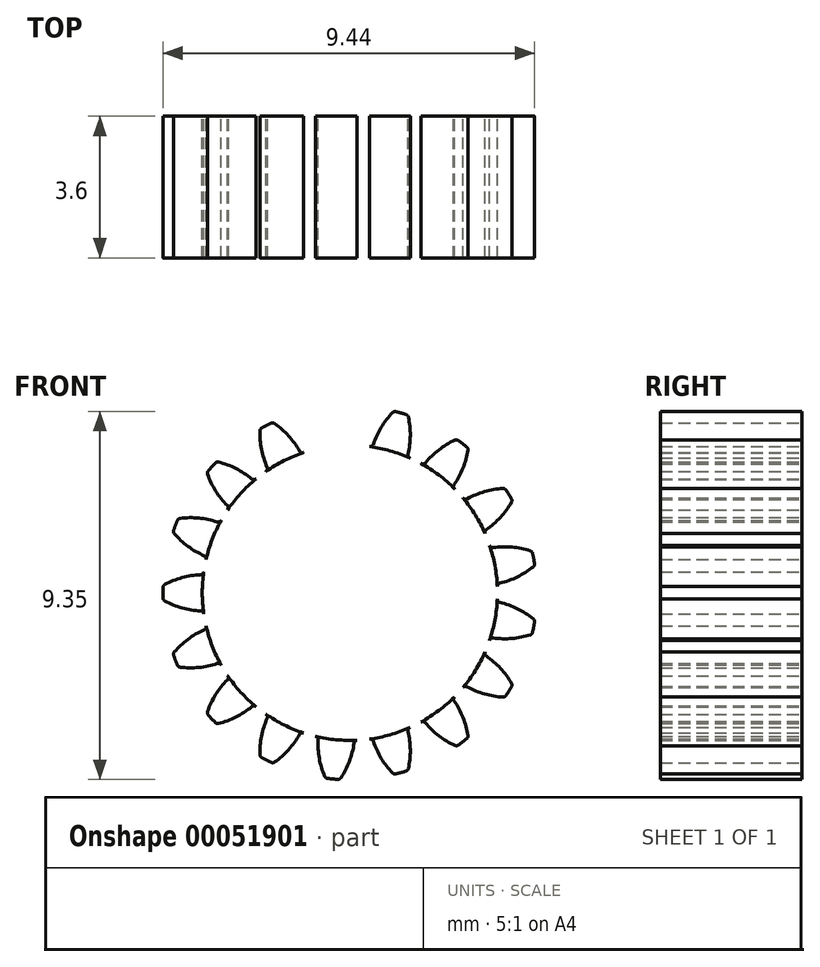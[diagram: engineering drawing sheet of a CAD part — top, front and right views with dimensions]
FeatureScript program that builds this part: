
annotation { "Feature Type Name" : "Feature", "Feature Type Description" : "" }
export const myFeature = defineFeature(function(context is Context, id is Id, definition is map)
    precondition{}
    {
        {
            var Q0;
            Q0=qCreatedBy(makeId("Front.planeOp"),FACE);
            var sketch = newSketch(context, id + "F0", { "sketchPlane" : qUnion([Q0])});
            skCircle(sketch, "E0", {"center": v(0, 0) * mm, "radius": 3.75 * mm, "construction": true});
            skCircle(sketch, "E1", {"center": v(0, 0) * mm, "radius": 4.25 * mm, "construction": true});
            skCircle(sketch, "E2", {"center": v(0, 0) * mm, "radius": 4.75 * mm, "construction": true});
            skLineSegment(sketch, "E3", {"start": v(0, 0) * mm, "end": v(0, 10.28) * mm, "construction": true});
            skLineSegment(sketch, "E4", {"start": v(0, 0) * mm, "end": v(-1.03, 11.12) * mm, "construction": true});
            skLineSegment(sketch, "E5", {"start": v(0, 4.25) * mm, "end": v(-15.76, 4.25) * mm, "construction": true});
            skLineSegment(sketch, "E6", {"start": v(0, 4.25) * mm, "end": v(-14.39, -0.99) * mm, "construction": true});
            skCircle(sketch, "E7", {"center": v(0, 4.25) * mm, "radius": 2.12 * mm, "construction": true});
            skCircle(sketch, "E8", {"center": v(-2, 3.52) * mm, "radius": 2.12 * mm, "construction": true});
            skArc(sketch, "E9", {"start": v(-0.23, 4.7) * mm, "mid": v(-0.01, 4.28) * mm, "end": v(0.1, 3.82) * mm});
            skArc(sketch, "E10.MirrorCS", {"start": v(-0.64, 4.66) * mm, "mid": v(-0.78, 4.2) * mm, "end": v(-0.8, 3.73) * mm});
            skArc(sketch, "E11", {"start": v(-0.57, 4.72) * mm, "mid": v(-0.44, 4.73) * mm, "end": v(-0.3, 4.74) * mm});
            skArc(sketch, "E12", {"start": v(-0.87, 3.65) * mm, "mid": v(0.35, -3.73) * mm, "end": v(0.19, 3.75) * mm});
            skPoint(sketch, "E13.visualSharp", {"position": v(-0.8, 3.66) * mm});
            skArc(sketch, "E13.filletArc", {"start": v(-0.87, 3.65) * mm, "mid": v(-0.82, 3.68) * mm, "end": v(-0.8, 3.73) * mm});
            skPoint(sketch, "E14.visualSharp", {"position": v(-0.62, 4.7) * mm});
            skArc(sketch, "E14.filletArc", {"start": v(-0.57, 4.72) * mm, "mid": v(-0.61, 4.7) * mm, "end": v(-0.64, 4.66) * mm});
            skPoint(sketch, "E15.visualSharp", {"position": v(-0.26, 4.74) * mm});
            skArc(sketch, "E15.filletArc", {"start": v(-0.23, 4.7) * mm, "mid": v(-0.26, 4.73) * mm, "end": v(-0.3, 4.74) * mm});
            skPoint(sketch, "E16.visualSharp", {"position": v(0.12, 3.75) * mm});
            skArc(sketch, "E16.filletArc", {"start": v(0.1, 3.82) * mm, "mid": v(0.13, 3.77) * mm, "end": v(0.19, 3.75) * mm});
            skArc(sketch, "E17.1.0", {"start": v(-2.13, 3.09) * mm, "mid": v(-2.1, 3.13) * mm, "end": v(-2.1, 3.19) * mm});
            skArc(sketch, "E17.1.1", {"start": v(-2.28, 4.12) * mm, "mid": v(-2.24, 3.64) * mm, "end": v(-2.1, 3.19) * mm});
            skArc(sketch, "E17.1.2", {"start": v(-2.24, 4.2) * mm, "mid": v(-2.27, 4.16) * mm, "end": v(-2.28, 4.12) * mm});
            skArc(sketch, "E17.1.3", {"start": v(-2.24, 4.2) * mm, "mid": v(-2.12, 4.25) * mm, "end": v(-2, 4.3) * mm});
            skArc(sketch, "E17.1.4", {"start": v(-1.91, 4.3) * mm, "mid": v(-1.95, 4.32) * mm, "end": v(-2, 4.3) * mm});
            skArc(sketch, "E17.1.5", {"start": v(-1.91, 4.3) * mm, "mid": v(-1.56, 3.99) * mm, "end": v(-1.28, 3.6) * mm});
            skArc(sketch, "E17.1.6", {"start": v(-1.28, 3.6) * mm, "mid": v(-1.24, 3.56) * mm, "end": v(-1.18, 3.56) * mm});
            skArc(sketch, "E17.2.0", {"start": v(-3.1, 2.1) * mm, "mid": v(-3.09, 2.16) * mm, "end": v(-3.11, 2.22) * mm});
            skArc(sketch, "E17.2.1", {"start": v(-3.61, 3.02) * mm, "mid": v(-3.4, 2.59) * mm, "end": v(-3.11, 2.22) * mm});
            skArc(sketch, "E17.2.2", {"start": v(-3.6, 3.1) * mm, "mid": v(-3.62, 3.06) * mm, "end": v(-3.61, 3.02) * mm});
            skArc(sketch, "E17.2.3", {"start": v(-3.6, 3.1) * mm, "mid": v(-3.51, 3.2) * mm, "end": v(-3.42, 3.3) * mm});
            skArc(sketch, "E17.2.4", {"start": v(-3.34, 3.32) * mm, "mid": v(-3.38, 3.32) * mm, "end": v(-3.42, 3.3) * mm});
            skArc(sketch, "E17.2.5", {"start": v(-3.34, 3.32) * mm, "mid": v(-2.9, 3.16) * mm, "end": v(-2.5, 2.9) * mm});
            skArc(sketch, "E17.2.6", {"start": v(-2.5, 2.9) * mm, "mid": v(-2.44, 2.87) * mm, "end": v(-2.38, 2.9) * mm});
            skArc(sketch, "E17.3.0", {"start": v(-3.65, 0.84) * mm, "mid": v(-3.66, 0.9) * mm, "end": v(-3.7, 0.94) * mm});
            skArc(sketch, "E17.3.1", {"start": v(-4.46, 1.5) * mm, "mid": v(-4.11, 1.18) * mm, "end": v(-3.7, 0.94) * mm});
            skArc(sketch, "E17.3.2", {"start": v(-4.48, 1.6) * mm, "mid": v(-4.48, 1.55) * mm, "end": v(-4.46, 1.5) * mm});
            skArc(sketch, "E17.3.3", {"start": v(-4.48, 1.6) * mm, "mid": v(-4.43, 1.72) * mm, "end": v(-4.38, 1.84) * mm});
            skArc(sketch, "E17.3.4", {"start": v(-4.31, 1.9) * mm, "mid": v(-4.35, 1.87) * mm, "end": v(-4.38, 1.84) * mm});
            skArc(sketch, "E17.3.5", {"start": v(-4.31, 1.9) * mm, "mid": v(-3.84, 1.9) * mm, "end": v(-3.37, 1.8) * mm});
            skArc(sketch, "E17.3.6", {"start": v(-3.37, 1.8) * mm, "mid": v(-3.31, 1.8) * mm, "end": v(-3.27, 1.84) * mm});
            skArc(sketch, "E17.4.0", {"start": v(-3.71, -0.53) * mm, "mid": v(-3.74, -0.48) * mm, "end": v(-3.8, -0.46) * mm});
            skArc(sketch, "E17.4.1", {"start": v(-4.7, -0.2) * mm, "mid": v(-4.26, -0.38) * mm, "end": v(-3.8, -0.46) * mm});
            skArc(sketch, "E17.4.2", {"start": v(-4.75, -0.13) * mm, "mid": v(-4.74, -0.18) * mm, "end": v(-4.7, -0.2) * mm});
            skArc(sketch, "E17.4.3", {"start": v(-4.75, -0.13) * mm, "mid": v(-4.75, 0) * mm, "end": v(-4.75, 0.13) * mm});
            skArc(sketch, "E17.4.4", {"start": v(-4.7, 0.2) * mm, "mid": v(-4.74, 0.18) * mm, "end": v(-4.75, 0.13) * mm});
            skArc(sketch, "E17.4.5", {"start": v(-4.7, 0.2) * mm, "mid": v(-4.26, 0.38) * mm, "end": v(-3.8, 0.46) * mm});
            skArc(sketch, "E17.4.6", {"start": v(-3.8, 0.46) * mm, "mid": v(-3.74, 0.48) * mm, "end": v(-3.71, 0.53) * mm});
            skArc(sketch, "E17.5.0", {"start": v(-3.27, -1.84) * mm, "mid": v(-3.31, -1.8) * mm, "end": v(-3.37, -1.8) * mm});
            skArc(sketch, "E17.5.1", {"start": v(-4.31, -1.9) * mm, "mid": v(-3.84, -1.9) * mm, "end": v(-3.37, -1.8) * mm});
            skArc(sketch, "E17.5.2", {"start": v(-4.38, -1.84) * mm, "mid": v(-4.35, -1.87) * mm, "end": v(-4.31, -1.9) * mm});
            skArc(sketch, "E17.5.3", {"start": v(-4.38, -1.84) * mm, "mid": v(-4.43, -1.72) * mm, "end": v(-4.48, -1.6) * mm});
            skArc(sketch, "E17.5.4", {"start": v(-4.46, -1.5) * mm, "mid": v(-4.48, -1.55) * mm, "end": v(-4.48, -1.6) * mm});
            skArc(sketch, "E17.5.5", {"start": v(-4.46, -1.5) * mm, "mid": v(-4.11, -1.18) * mm, "end": v(-3.7, -0.94) * mm});
            skArc(sketch, "E17.5.6", {"start": v(-3.7, -0.94) * mm, "mid": v(-3.66, -0.9) * mm, "end": v(-3.65, -0.84) * mm});
            skArc(sketch, "E17.6.0", {"start": v(-2.38, -2.9) * mm, "mid": v(-2.44, -2.87) * mm, "end": v(-2.5, -2.9) * mm});
            skArc(sketch, "E17.6.1", {"start": v(-3.34, -3.32) * mm, "mid": v(-2.9, -3.16) * mm, "end": v(-2.5, -2.9) * mm});
            skArc(sketch, "E17.6.2", {"start": v(-3.42, -3.3) * mm, "mid": v(-3.38, -3.32) * mm, "end": v(-3.34, -3.32) * mm});
            skArc(sketch, "E17.6.3", {"start": v(-3.42, -3.3) * mm, "mid": v(-3.51, -3.2) * mm, "end": v(-3.6, -3.1) * mm});
            skArc(sketch, "E17.6.4", {"start": v(-3.61, -3.02) * mm, "mid": v(-3.62, -3.06) * mm, "end": v(-3.6, -3.1) * mm});
            skArc(sketch, "E17.6.5", {"start": v(-3.61, -3.02) * mm, "mid": v(-3.4, -2.59) * mm, "end": v(-3.11, -2.22) * mm});
            skArc(sketch, "E17.6.6", {"start": v(-3.11, -2.22) * mm, "mid": v(-3.09, -2.16) * mm, "end": v(-3.1, -2.1) * mm});
            skArc(sketch, "E17.7.0", {"start": v(-1.18, -3.56) * mm, "mid": v(-1.24, -3.56) * mm, "end": v(-1.28, -3.6) * mm});
            skArc(sketch, "E17.7.1", {"start": v(-1.91, -4.3) * mm, "mid": v(-1.56, -3.99) * mm, "end": v(-1.28, -3.6) * mm});
            skArc(sketch, "E17.7.2", {"start": v(-2, -4.3) * mm, "mid": v(-1.95, -4.32) * mm, "end": v(-1.91, -4.3) * mm});
            skArc(sketch, "E17.7.3", {"start": v(-2, -4.3) * mm, "mid": v(-2.12, -4.25) * mm, "end": v(-2.24, -4.2) * mm});
            skArc(sketch, "E17.7.4", {"start": v(-2.28, -4.12) * mm, "mid": v(-2.27, -4.16) * mm, "end": v(-2.24, -4.2) * mm});
            skArc(sketch, "E17.7.5", {"start": v(-2.28, -4.12) * mm, "mid": v(-2.24, -3.64) * mm, "end": v(-2.1, -3.19) * mm});
            skArc(sketch, "E17.7.6", {"start": v(-2.1, -3.19) * mm, "mid": v(-2.1, -3.13) * mm, "end": v(-2.13, -3.09) * mm});
            skArc(sketch, "E17.8.0", {"start": v(0.19, -3.75) * mm, "mid": v(0.13, -3.77) * mm, "end": v(0.1, -3.82) * mm});
            skArc(sketch, "E17.8.1", {"start": v(-0.23, -4.7) * mm, "mid": v(-0.01, -4.28) * mm, "end": v(0.1, -3.82) * mm});
            skArc(sketch, "E17.8.2", {"start": v(-0.3, -4.74) * mm, "mid": v(-0.26, -4.73) * mm, "end": v(-0.23, -4.7) * mm});
            skArc(sketch, "E17.8.3", {"start": v(-0.3, -4.74) * mm, "mid": v(-0.44, -4.73) * mm, "end": v(-0.57, -4.72) * mm});
            skArc(sketch, "E17.8.4", {"start": v(-0.64, -4.66) * mm, "mid": v(-0.61, -4.7) * mm, "end": v(-0.57, -4.72) * mm});
            skArc(sketch, "E17.8.5", {"start": v(-0.64, -4.66) * mm, "mid": v(-0.78, -4.2) * mm, "end": v(-0.8, -3.73) * mm});
            skArc(sketch, "E17.8.6", {"start": v(-0.8, -3.73) * mm, "mid": v(-0.82, -3.68) * mm, "end": v(-0.87, -3.65) * mm});
            skArc(sketch, "E17.9.0", {"start": v(1.53, -3.42) * mm, "mid": v(1.49, -3.46) * mm, "end": v(1.48, -3.52) * mm});
            skArc(sketch, "E17.9.1", {"start": v(1.49, -4.47) * mm, "mid": v(1.54, -4) * mm, "end": v(1.48, -3.52) * mm});
            skArc(sketch, "E17.9.2", {"start": v(1.43, -4.53) * mm, "mid": v(1.46, -4.5) * mm, "end": v(1.49, -4.47) * mm});
            skArc(sketch, "E17.9.3", {"start": v(1.43, -4.53) * mm, "mid": v(1.3, -4.57) * mm, "end": v(1.17, -4.6) * mm});
            skArc(sketch, "E17.9.4", {"start": v(1.09, -4.58) * mm, "mid": v(1.13, -4.6) * mm, "end": v(1.17, -4.6) * mm});
            skArc(sketch, "E17.9.5", {"start": v(1.09, -4.58) * mm, "mid": v(0.8, -4.2) * mm, "end": v(0.6, -3.77) * mm});
            skArc(sketch, "E17.9.6", {"start": v(0.6, -3.77) * mm, "mid": v(0.56, -3.73) * mm, "end": v(0.5, -3.72) * mm});
            skArc(sketch, "E17.10.0", {"start": v(2.66, -2.64) * mm, "mid": v(2.64, -2.7) * mm, "end": v(2.65, -2.75) * mm});
            skArc(sketch, "E17.10.1", {"start": v(3, -3.63) * mm, "mid": v(2.87, -3.17) * mm, "end": v(2.65, -2.75) * mm});
            skArc(sketch, "E17.10.2", {"start": v(2.97, -3.7) * mm, "mid": v(3, -3.67) * mm, "end": v(3, -3.63) * mm});
            skArc(sketch, "E17.10.3", {"start": v(2.97, -3.7) * mm, "mid": v(2.86, -3.8) * mm, "end": v(2.75, -3.87) * mm});
            skArc(sketch, "E17.10.4", {"start": v(2.67, -3.88) * mm, "mid": v(2.71, -3.88) * mm, "end": v(2.75, -3.87) * mm});
            skArc(sketch, "E17.10.5", {"start": v(2.67, -3.88) * mm, "mid": v(2.26, -3.63) * mm, "end": v(1.92, -3.3) * mm});
            skArc(sketch, "E17.10.6", {"start": v(1.92, -3.3) * mm, "mid": v(1.87, -3.27) * mm, "end": v(1.81, -3.28) * mm});
            skArc(sketch, "E17.11.0", {"start": v(3.44, -1.5) * mm, "mid": v(3.43, -1.56) * mm, "end": v(3.47, -1.6) * mm});
            skArc(sketch, "E17.11.1", {"start": v(4.1, -2.3) * mm, "mid": v(3.83, -1.92) * mm, "end": v(3.47, -1.6) * mm});
            skArc(sketch, "E17.11.2", {"start": v(4.1, -2.39) * mm, "mid": v(4.12, -2.34) * mm, "end": v(4.1, -2.3) * mm});
            skArc(sketch, "E17.11.3", {"start": v(4.1, -2.39) * mm, "mid": v(4.04, -2.5) * mm, "end": v(3.97, -2.61) * mm});
            skArc(sketch, "E17.11.4", {"start": v(3.9, -2.65) * mm, "mid": v(3.93, -2.64) * mm, "end": v(3.97, -2.61) * mm});
            skArc(sketch, "E17.11.5", {"start": v(3.9, -2.65) * mm, "mid": v(3.42, -2.57) * mm, "end": v(2.98, -2.39) * mm});
            skArc(sketch, "E17.11.6", {"start": v(2.98, -2.39) * mm, "mid": v(2.93, -2.38) * mm, "end": v(2.88, -2.4) * mm});
            skArc(sketch, "E17.12.0", {"start": v(3.75, -0.16) * mm, "mid": v(3.76, -0.21) * mm, "end": v(3.81, -0.25) * mm});
            skArc(sketch, "E17.12.1", {"start": v(4.66, -0.66) * mm, "mid": v(4.26, -0.4) * mm, "end": v(3.81, -0.25) * mm});
            skArc(sketch, "E17.12.2", {"start": v(4.7, -0.74) * mm, "mid": v(4.69, -0.7) * mm, "end": v(4.66, -0.66) * mm});
            skArc(sketch, "E17.12.3", {"start": v(4.7, -0.74) * mm, "mid": v(4.67, -0.87) * mm, "end": v(4.64, -1) * mm});
            skArc(sketch, "E17.12.4", {"start": v(4.59, -1.07) * mm, "mid": v(4.62, -1.04) * mm, "end": v(4.64, -1) * mm});
            skArc(sketch, "E17.12.5", {"start": v(4.59, -1.07) * mm, "mid": v(4.12, -1.16) * mm, "end": v(3.64, -1.15) * mm});
            skArc(sketch, "E17.12.6", {"start": v(3.64, -1.15) * mm, "mid": v(3.59, -1.16) * mm, "end": v(3.55, -1.2) * mm});
            skArc(sketch, "E17.13.0", {"start": v(3.55, 1.2) * mm, "mid": v(3.59, 1.16) * mm, "end": v(3.64, 1.15) * mm});
            skArc(sketch, "E17.13.1", {"start": v(4.59, 1.07) * mm, "mid": v(4.12, 1.16) * mm, "end": v(3.64, 1.15) * mm});
            skArc(sketch, "E17.13.2", {"start": v(4.64, 1) * mm, "mid": v(4.62, 1.04) * mm, "end": v(4.59, 1.07) * mm});
            skArc(sketch, "E17.13.3", {"start": v(4.64, 1) * mm, "mid": v(4.67, 0.87) * mm, "end": v(4.7, 0.74) * mm});
            skArc(sketch, "E17.13.4", {"start": v(4.66, 0.66) * mm, "mid": v(4.69, 0.7) * mm, "end": v(4.7, 0.74) * mm});
            skArc(sketch, "E17.13.5", {"start": v(4.66, 0.66) * mm, "mid": v(4.26, 0.4) * mm, "end": v(3.81, 0.25) * mm});
            skArc(sketch, "E17.13.6", {"start": v(3.81, 0.25) * mm, "mid": v(3.76, 0.21) * mm, "end": v(3.75, 0.16) * mm});
            skArc(sketch, "E17.14.0", {"start": v(2.88, 2.4) * mm, "mid": v(2.93, 2.38) * mm, "end": v(2.98, 2.39) * mm});
            skArc(sketch, "E17.14.1", {"start": v(3.9, 2.65) * mm, "mid": v(3.42, 2.57) * mm, "end": v(2.98, 2.39) * mm});
            skArc(sketch, "E17.14.2", {"start": v(3.97, 2.61) * mm, "mid": v(3.93, 2.64) * mm, "end": v(3.9, 2.65) * mm});
            skArc(sketch, "E17.14.3", {"start": v(3.97, 2.61) * mm, "mid": v(4.04, 2.5) * mm, "end": v(4.1, 2.39) * mm});
            skArc(sketch, "E17.14.4", {"start": v(4.1, 2.3) * mm, "mid": v(4.12, 2.34) * mm, "end": v(4.1, 2.39) * mm});
            skArc(sketch, "E17.14.5", {"start": v(4.1, 2.3) * mm, "mid": v(3.83, 1.92) * mm, "end": v(3.47, 1.6) * mm});
            skArc(sketch, "E17.14.6", {"start": v(3.47, 1.6) * mm, "mid": v(3.43, 1.56) * mm, "end": v(3.44, 1.5) * mm});
            skArc(sketch, "E17.15.0", {"start": v(1.81, 3.28) * mm, "mid": v(1.87, 3.27) * mm, "end": v(1.92, 3.3) * mm});
            skArc(sketch, "E17.15.1", {"start": v(2.67, 3.88) * mm, "mid": v(2.26, 3.63) * mm, "end": v(1.92, 3.3) * mm});
            skArc(sketch, "E17.15.2", {"start": v(2.75, 3.87) * mm, "mid": v(2.71, 3.88) * mm, "end": v(2.67, 3.88) * mm});
            skArc(sketch, "E17.15.3", {"start": v(2.75, 3.87) * mm, "mid": v(2.86, 3.8) * mm, "end": v(2.97, 3.7) * mm});
            skArc(sketch, "E17.15.4", {"start": v(3, 3.63) * mm, "mid": v(3, 3.67) * mm, "end": v(2.97, 3.7) * mm});
            skArc(sketch, "E17.15.5", {"start": v(3, 3.63) * mm, "mid": v(2.87, 3.17) * mm, "end": v(2.65, 2.75) * mm});
            skArc(sketch, "E17.15.6", {"start": v(2.65, 2.75) * mm, "mid": v(2.64, 2.7) * mm, "end": v(2.66, 2.64) * mm});
            skArc(sketch, "E17.16.0", {"start": v(0.5, 3.72) * mm, "mid": v(0.56, 3.73) * mm, "end": v(0.6, 3.77) * mm});
            skArc(sketch, "E17.16.1", {"start": v(1.09, 4.58) * mm, "mid": v(0.8, 4.2) * mm, "end": v(0.6, 3.77) * mm});
            skArc(sketch, "E17.16.2", {"start": v(1.17, 4.6) * mm, "mid": v(1.13, 4.6) * mm, "end": v(1.09, 4.58) * mm});
            skArc(sketch, "E17.16.3", {"start": v(1.17, 4.6) * mm, "mid": v(1.3, 4.57) * mm, "end": v(1.43, 4.53) * mm});
            skArc(sketch, "E17.16.4", {"start": v(1.49, 4.47) * mm, "mid": v(1.46, 4.5) * mm, "end": v(1.43, 4.53) * mm});
            skArc(sketch, "E17.16.5", {"start": v(1.49, 4.47) * mm, "mid": v(1.54, 4) * mm, "end": v(1.48, 3.52) * mm});
            skArc(sketch, "E17.16.6", {"start": v(1.48, 3.52) * mm, "mid": v(1.49, 3.46) * mm, "end": v(1.53, 3.42) * mm});
            skSolve(sketch);
        }
        {
            var Q0;
            Q0=makeQuery(id+"F0.imprint","IMPRINT",FACE,{"disambiguationData":[TD([[makeQuery(id+"F0.imprint","IMPRINT",EDGE,{"derivedFrom":sQuery(id+"F0.wireOp",EDGE,"E9")}),-1.0]])]});
            var Q1;
            {var subQ0=sQuery(id+"F0.wireOp",EDGE,"E17.1.0");Q1=makeQuery(id+"F0.imprint","IMPRINT",FACE,{"disambiguationData":[TD([[makeQuery(id+"F0.imprint","IMPRINT",EDGE,{"derivedFrom":subQ0}),-1.0]])]});}
            var Q2;
            {var subQ0=sQuery(id+"F0.wireOp",EDGE,"E17.2.0");Q2=makeQuery(id+"F0.imprint","IMPRINT",FACE,{"disambiguationData":[TD([[makeQuery(id+"F0.imprint","IMPRINT",EDGE,{"derivedFrom":subQ0}),-1.0]])]});}
            var Q3;
            {var subQ0=sQuery(id+"F0.wireOp",EDGE,"E17.3.0");Q3=makeQuery(id+"F0.imprint","IMPRINT",FACE,{"disambiguationData":[TD([[makeQuery(id+"F0.imprint","IMPRINT",EDGE,{"derivedFrom":subQ0}),-1.0]])]});}
            var Q4;
            {var subQ0=sQuery(id+"F0.wireOp",EDGE,"E17.4.0");Q4=makeQuery(id+"F0.imprint","IMPRINT",FACE,{"disambiguationData":[TD([[makeQuery(id+"F0.imprint","IMPRINT",EDGE,{"derivedFrom":subQ0}),-1.0]])]});}
            var Q5;
            {var subQ0=sQuery(id+"F0.wireOp",EDGE,"E17.16.0");Q5=makeQuery(id+"F0.imprint","IMPRINT",FACE,{"disambiguationData":[TD([[makeQuery(id+"F0.imprint","IMPRINT",EDGE,{"derivedFrom":subQ0}),-1.0]])]});}
            var Q6;
            {var subQ0=sQuery(id+"F0.wireOp",EDGE,"E17.15.0");Q6=makeQuery(id+"F0.imprint","IMPRINT",FACE,{"disambiguationData":[TD([[makeQuery(id+"F0.imprint","IMPRINT",EDGE,{"derivedFrom":subQ0}),-1.0]])]});}
            var Q7;
            {var subQ1=sQuery(id+"F0.wireOp",EDGE,"E17.14.0");Q7=makeQuery(id+"F0.imprint","IMPRINT",FACE,{"disambiguationData":[TD([[makeQuery(id+"F0.imprint","IMPRINT",EDGE,{"derivedFrom":subQ1}),-1.0]])]});}
            var Q8;
            {var subQ0=sQuery(id+"F0.wireOp",EDGE,"E17.13.0");Q8=makeQuery(id+"F0.imprint","IMPRINT",FACE,{"disambiguationData":[TD([[makeQuery(id+"F0.imprint","IMPRINT",EDGE,{"derivedFrom":subQ0}),-1.0]])]});}
            var Q9;
            {var subQ1=sQuery(id+"F0.wireOp",EDGE,"E17.12.0");Q9=makeQuery(id+"F0.imprint","IMPRINT",FACE,{"disambiguationData":[TD([[makeQuery(id+"F0.imprint","IMPRINT",EDGE,{"derivedFrom":subQ1}),-1.0]])]});}
            var Q10;
            {var subQ0=sQuery(id+"F0.wireOp",EDGE,"E17.11.0");Q10=makeQuery(id+"F0.imprint","IMPRINT",FACE,{"disambiguationData":[TD([[makeQuery(id+"F0.imprint","IMPRINT",EDGE,{"derivedFrom":subQ0}),-1.0]])]});}
            var Q11;
            {var subQ0=sQuery(id+"F0.wireOp",EDGE,"E17.10.0");Q11=makeQuery(id+"F0.imprint","IMPRINT",FACE,{"disambiguationData":[TD([[makeQuery(id+"F0.imprint","IMPRINT",EDGE,{"derivedFrom":subQ0}),-1.0]])]});}
            var Q12;
            {var subQ0=sQuery(id+"F0.wireOp",EDGE,"E17.9.0");Q12=makeQuery(id+"F0.imprint","IMPRINT",FACE,{"disambiguationData":[TD([[makeQuery(id+"F0.imprint","IMPRINT",EDGE,{"derivedFrom":subQ0}),-1.0]])]});}
            var Q13;
            {var subQ0=sQuery(id+"F0.wireOp",EDGE,"E17.8.0");Q13=makeQuery(id+"F0.imprint","IMPRINT",FACE,{"disambiguationData":[TD([[makeQuery(id+"F0.imprint","IMPRINT",EDGE,{"derivedFrom":subQ0}),-1.0]])]});}
            var Q14;
            {var subQ0=sQuery(id+"F0.wireOp",EDGE,"E17.7.0");Q14=makeQuery(id+"F0.imprint","IMPRINT",FACE,{"disambiguationData":[TD([[makeQuery(id+"F0.imprint","IMPRINT",EDGE,{"derivedFrom":subQ0}),-1.0]])]});}
            var Q15;
            {var subQ0=sQuery(id+"F0.wireOp",EDGE,"E17.6.0");Q15=makeQuery(id+"F0.imprint","IMPRINT",FACE,{"disambiguationData":[TD([[makeQuery(id+"F0.imprint","IMPRINT",EDGE,{"derivedFrom":subQ0}),-1.0]])]});}
            var Q16;
            {var subQ0=sQuery(id+"F0.wireOp",EDGE,"E17.5.0");Q16=makeQuery(id+"F0.imprint","IMPRINT",FACE,{"disambiguationData":[TD([[makeQuery(id+"F0.imprint","IMPRINT",EDGE,{"derivedFrom":subQ0}),-1.0]])]});}
            extrude(context, id + "F1", {"entities" : qUnion([Q0, Q1, Q2, Q3, Q4, Q5, Q6, Q7, Q8, Q9, Q10, Q11, Q12, Q13, Q14, Q15, Q16]), "depth" : 3.6 * mm});
        }
        {
            var Q0;
            Q0=makeQuery(id+"F1.opExtrude","CAP_FACE",FACE,{"disambiguationData":[OSD([sQuery(id+"F0.wireOp",EDGE,"E9"),sQuery(id+"F0.wireOp",EDGE,"E10.MirrorCS"),sQuery(id+"F0.wireOp",EDGE,"E11"),sQuery(id+"F0.wireOp",EDGE,"E12"),sQuery(id+"F0.wireOp",EDGE,"E13.filletArc"),sQuery(id+"F0.wireOp",EDGE,"E14.filletArc"),sQuery(id+"F0.wireOp",EDGE,"E15.filletArc"),sQuery(id+"F0.wireOp",EDGE,"E16.filletArc"),sQuery(id+"F0.wireOp",EDGE,"E17.1.0"),sQuery(id+"F0.wireOp",EDGE,"E17.1.1"),sQuery(id+"F0.wireOp",EDGE,"E17.1.2"),sQuery(id+"F0.wireOp",EDGE,"E17.1.3"),sQuery(id+"F0.wireOp",EDGE,"E17.1.4"),sQuery(id+"F0.wireOp",EDGE,"E17.1.5"),sQuery(id+"F0.wireOp",EDGE,"E17.1.6"),sQuery(id+"F0.wireOp",EDGE,"E17.2.0"),sQuery(id+"F0.wireOp",EDGE,"E17.2.1"),sQuery(id+"F0.wireOp",EDGE,"E17.2.2"),sQuery(id+"F0.wireOp",EDGE,"E17.2.3"),sQuery(id+"F0.wireOp",EDGE,"E17.2.4"),sQuery(id+"F0.wireOp",EDGE,"E17.2.5"),sQuery(id+"F0.wireOp",EDGE,"E17.2.6"),sQuery(id+"F0.wireOp",EDGE,"E17.3.0"),sQuery(id+"F0.wireOp",EDGE,"E17.3.1"),sQuery(id+"F0.wireOp",EDGE,"E17.3.2"),sQuery(id+"F0.wireOp",EDGE,"E17.3.3"),sQuery(id+"F0.wireOp",EDGE,"E17.3.4"),sQuery(id+"F0.wireOp",EDGE,"E17.3.5"),sQuery(id+"F0.wireOp",EDGE,"E17.3.6"),sQuery(id+"F0.wireOp",EDGE,"E17.4.0"),sQuery(id+"F0.wireOp",EDGE,"E17.4.1"),sQuery(id+"F0.wireOp",EDGE,"E17.4.2"),sQuery(id+"F0.wireOp",EDGE,"E17.4.3"),sQuery(id+"F0.wireOp",EDGE,"E17.4.4"),sQuery(id+"F0.wireOp",EDGE,"E17.4.5"),sQuery(id+"F0.wireOp",EDGE,"E17.4.6"),sQuery(id+"F0.wireOp",EDGE,"E17.5.0"),sQuery(id+"F0.wireOp",EDGE,"E17.5.1"),sQuery(id+"F0.wireOp",EDGE,"E17.5.2"),sQuery(id+"F0.wireOp",EDGE,"E17.5.3"),sQuery(id+"F0.wireOp",EDGE,"E17.5.4"),sQuery(id+"F0.wireOp",EDGE,"E17.5.5"),sQuery(id+"F0.wireOp",EDGE,"E17.5.6"),sQuery(id+"F0.wireOp",EDGE,"E17.6.0"),sQuery(id+"F0.wireOp",EDGE,"E17.6.1"),sQuery(id+"F0.wireOp",EDGE,"E17.6.2"),sQuery(id+"F0.wireOp",EDGE,"E17.6.3"),sQuery(id+"F0.wireOp",EDGE,"E17.6.4"),sQuery(id+"F0.wireOp",EDGE,"E17.6.5"),sQuery(id+"F0.wireOp",EDGE,"E17.6.6"),sQuery(id+"F0.wireOp",EDGE,"E17.7.0"),sQuery(id+"F0.wireOp",EDGE,"E17.7.1"),sQuery(id+"F0.wireOp",EDGE,"E17.7.2"),sQuery(id+"F0.wireOp",EDGE,"E17.7.3"),sQuery(id+"F0.wireOp",EDGE,"E17.7.4"),sQuery(id+"F0.wireOp",EDGE,"E17.7.5"),sQuery(id+"F0.wireOp",EDGE,"E17.7.6"),sQuery(id+"F0.wireOp",EDGE,"E17.8.0"),sQuery(id+"F0.wireOp",EDGE,"E17.8.1"),sQuery(id+"F0.wireOp",EDGE,"E17.8.2"),sQuery(id+"F0.wireOp",EDGE,"E17.8.3"),sQuery(id+"F0.wireOp",EDGE,"E17.8.4"),sQuery(id+"F0.wireOp",EDGE,"E17.8.5"),sQuery(id+"F0.wireOp",EDGE,"E17.8.6"),sQuery(id+"F0.wireOp",EDGE,"E17.9.0"),sQuery(id+"F0.wireOp",EDGE,"E17.9.1"),sQuery(id+"F0.wireOp",EDGE,"E17.9.2"),sQuery(id+"F0.wireOp",EDGE,"E17.9.3"),sQuery(id+"F0.wireOp",EDGE,"E17.9.4"),sQuery(id+"F0.wireOp",EDGE,"E17.9.5"),sQuery(id+"F0.wireOp",EDGE,"E17.9.6"),sQuery(id+"F0.wireOp",EDGE,"E17.10.0"),sQuery(id+"F0.wireOp",EDGE,"E17.10.1"),sQuery(id+"F0.wireOp",EDGE,"E17.10.2"),sQuery(id+"F0.wireOp",EDGE,"E17.10.3"),sQuery(id+"F0.wireOp",EDGE,"E17.10.4"),sQuery(id+"F0.wireOp",EDGE,"E17.10.5"),sQuery(id+"F0.wireOp",EDGE,"E17.10.6"),sQuery(id+"F0.wireOp",EDGE,"E17.11.0"),sQuery(id+"F0.wireOp",EDGE,"E17.11.1"),sQuery(id+"F0.wireOp",EDGE,"E17.11.2"),sQuery(id+"F0.wireOp",EDGE,"E17.11.3"),sQuery(id+"F0.wireOp",EDGE,"E17.11.4"),sQuery(id+"F0.wireOp",EDGE,"E17.11.5"),sQuery(id+"F0.wireOp",EDGE,"E17.11.6"),sQuery(id+"F0.wireOp",EDGE,"E17.12.0"),sQuery(id+"F0.wireOp",EDGE,"E17.12.1"),sQuery(id+"F0.wireOp",EDGE,"E17.12.2"),sQuery(id+"F0.wireOp",EDGE,"E17.12.3"),sQuery(id+"F0.wireOp",EDGE,"E17.12.4"),sQuery(id+"F0.wireOp",EDGE,"E17.12.5"),sQuery(id+"F0.wireOp",EDGE,"E17.12.6"),sQuery(id+"F0.wireOp",EDGE,"E17.13.0"),sQuery(id+"F0.wireOp",EDGE,"E17.13.1"),sQuery(id+"F0.wireOp",EDGE,"E17.13.2"),sQuery(id+"F0.wireOp",EDGE,"E17.13.3"),sQuery(id+"F0.wireOp",EDGE,"E17.13.4"),sQuery(id+"F0.wireOp",EDGE,"E17.13.5"),sQuery(id+"F0.wireOp",EDGE,"E17.13.6"),sQuery(id+"F0.wireOp",EDGE,"E17.14.0"),sQuery(id+"F0.wireOp",EDGE,"E17.14.1"),sQuery(id+"F0.wireOp",EDGE,"E17.14.2"),sQuery(id+"F0.wireOp",EDGE,"E17.14.3"),sQuery(id+"F0.wireOp",EDGE,"E17.14.4"),sQuery(id+"F0.wireOp",EDGE,"E17.14.5"),sQuery(id+"F0.wireOp",EDGE,"E17.14.6"),sQuery(id+"F0.wireOp",EDGE,"E17.15.0"),sQuery(id+"F0.wireOp",EDGE,"E17.15.1"),sQuery(id+"F0.wireOp",EDGE,"E17.15.2"),sQuery(id+"F0.wireOp",EDGE,"E17.15.3"),sQuery(id+"F0.wireOp",EDGE,"E17.15.4"),sQuery(id+"F0.wireOp",EDGE,"E17.15.5"),sQuery(id+"F0.wireOp",EDGE,"E17.15.6"),sQuery(id+"F0.wireOp",EDGE,"E17.16.0"),sQuery(id+"F0.wireOp",EDGE,"E17.16.1"),sQuery(id+"F0.wireOp",EDGE,"E17.16.2"),sQuery(id+"F0.wireOp",EDGE,"E17.16.3"),sQuery(id+"F0.wireOp",EDGE,"E17.16.4"),sQuery(id+"F0.wireOp",EDGE,"E17.16.5"),sQuery(id+"F0.wireOp",EDGE,"E17.16.6")])],"isStart":false});
            var sketch = newSketch(context, id + "F2", { "sketchPlane" : qUnion([Q0])});
            skCircle(sketch, "E18", {"center": v(0, 0) * mm, "radius": 1 * mm});
            skSolve(sketch);
        }
        {
            var Q0;
            Q0=qSketchRegion(id+"F2",true);
            extrude(context, id + "F3", {"entities" : qUnion([Q0]), "operationType" : NewBodyOperationType.REMOVE, "endBound" : BoundingType.THROUGH_ALL, "oppositeDirection" : true, "depth" : 25 * mm});
        }
    });
